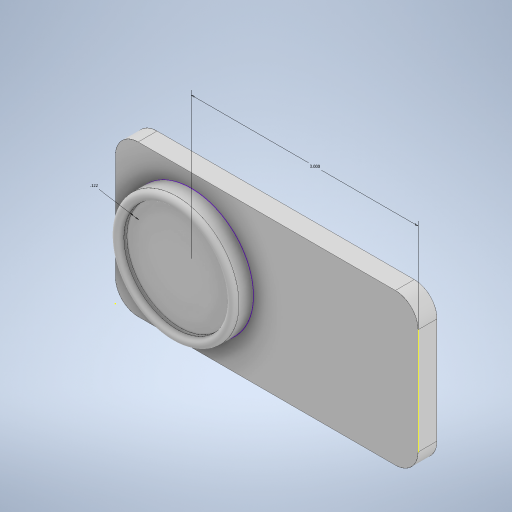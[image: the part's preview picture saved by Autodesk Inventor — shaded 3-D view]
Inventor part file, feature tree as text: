
AUTODESK INVENTOR PART (.ipt)
format: ipt  version: 2023.2 (Build 272271030, 271C)  size: 270,336 bytes
history: native  units: in
note: dims shown in document units (in); Inventor stores cm internally (conversion verified against a paired STEP export)
features: extrude x4, fillet x2, sketch x2
ambient origin geometry x8: Origin, YZ Plane, XZ Plane, XY Plane, X Axis, Y Axis, Z Axis, Center Point
bodies: Solid1 (feature_tree)
feature tree (8):
  extrude  "Extrusion1"  Depth=2.0in
  fillet  "Fillet1"  Radius=0.25in
  sketch  "Sketch2"  dims[d4=0.3in d5=3.0in d6=0.25in d7=0.0in d8=0.25in d9=0.0in d10=0.15in d11=0.0in d13=0.1218in d14=0.0609in]
  extrude  "Extrusion2"  Depth=0.0609in
  extrude  "Extrusion3"  Depth=0.25in TaperAngle=0.0deg
  extrude  "Extrusion4"  Depth=0.25in TaperAngle=0.0deg
  fillet  "Fillet3"  Radius=0.15in
  sketch  "Sketch1"  dims[d0=4.0in d1=2.0in d2=0.25in d3=0.0in]
